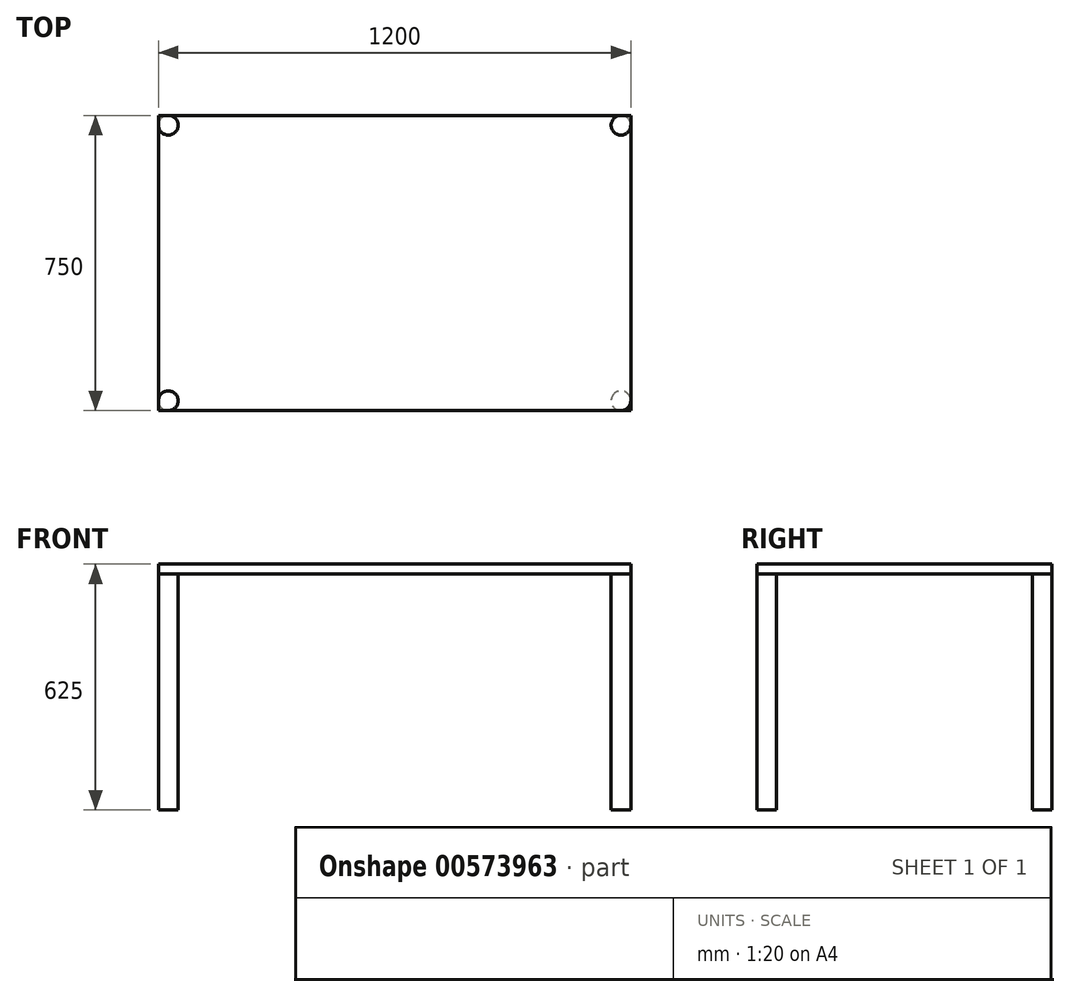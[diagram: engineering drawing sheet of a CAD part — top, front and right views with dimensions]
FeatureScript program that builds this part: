
annotation { "Feature Type Name" : "Feature", "Feature Type Description" : "" }
export const myFeature = defineFeature(function(context is Context, id is Id, definition is map)
    precondition{}
    {
        {
            var Q0;
            Q0=qCreatedBy(makeId("Top.planeOp"),FACE);
            cPlane(context, id + "F0", {"entities" : qUnion([Q0]), "cplaneType" : CPlaneType.OFFSET, "offset" : 600 * mm, "width" : 150 * mm, "height" : 150 * mm});
        }
        {
            var Q0;
            Q0=qCreatedBy(makeId("Top.planeOp"),FACE);
            var sketch = newSketch(context, id + "F1", { "sketchPlane" : qUnion([Q0])});
            skPoint(sketch, "E0.middle", {"position": v(0, 0) * mm});
            skCircle(sketch, "E1", {"center": v(-575, 350) * mm, "radius": 25 * mm});
            skCircle(sketch, "E2", {"center": v(-575, -350) * mm, "radius": 25 * mm});
            skCircle(sketch, "E3", {"center": v(575, -350) * mm, "radius": 25 * mm});
            skCircle(sketch, "E4", {"center": v(575, 350) * mm, "radius": 25 * mm});
            skSolve(sketch);
        }
        {
            var Q0;
            Q0=qCreatedBy(id+"F0.planeOp",FACE);
            var sketch = newSketch(context, id + "F2", { "sketchPlane" : qUnion([Q0])});
            skLineSegment(sketch, "E5.bottom", {"start": v(600, 375) * mm, "end": v(-600, 375) * mm});
            skLineSegment(sketch, "E5.top", {"start": v(600, -375) * mm, "end": v(-600, -375) * mm});
            skLineSegment(sketch, "E5.left", {"start": v(600, 375) * mm, "end": v(600, -375) * mm});
            skLineSegment(sketch, "E5.right", {"start": v(-600, 375) * mm, "end": v(-600, -375) * mm});
            skPoint(sketch, "E5.middle", {"position": v(0, 0) * mm});
            skSolve(sketch);
        }
        {
            var Q0;
            Q0 = qSketchRegion(id + "F1", true);
            extrude(context, id + "F3", {"entities" : qUnion([Q0]), "depth" : 600 * mm, "offsetDistance" : 25 * mm});
        }
        {
            var Q0;
            Q0 = qSketchRegion(id + "F2", true);
            extrude(context, id + "F4", {"entities" : qUnion([Q0]), "depth" : 25 * mm, "offsetDistance" : 25 * mm});
        }
    });
